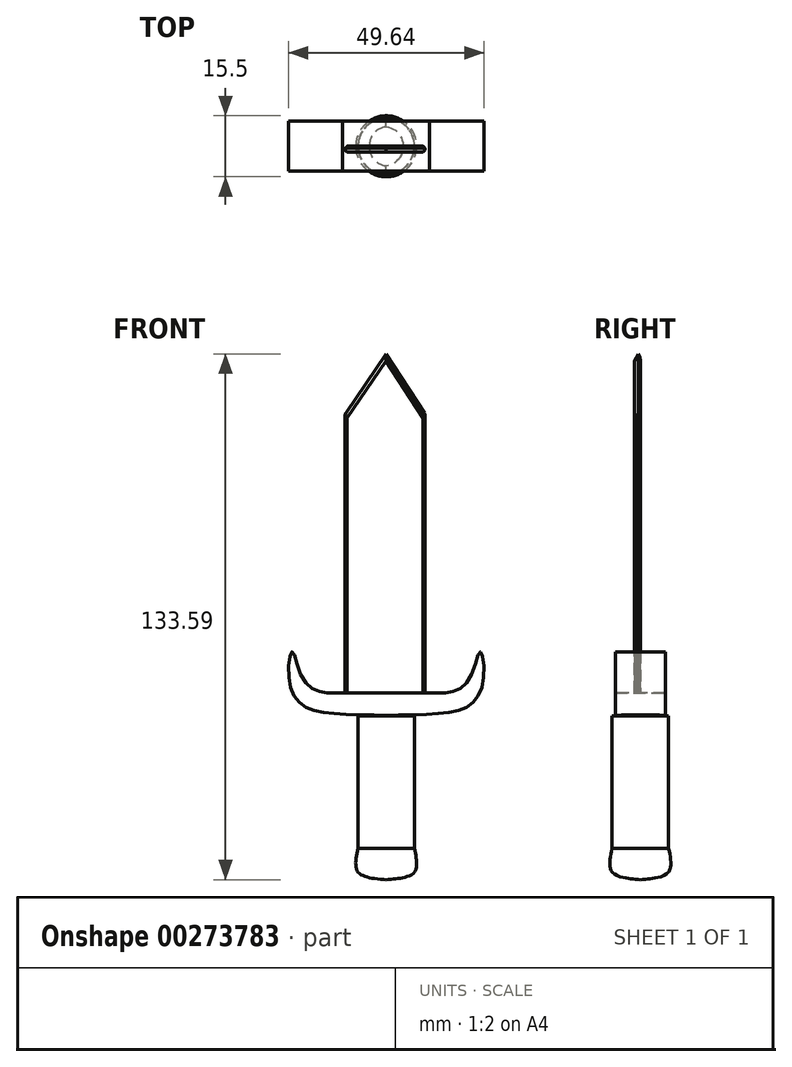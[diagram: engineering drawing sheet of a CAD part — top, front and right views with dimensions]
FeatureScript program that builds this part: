
annotation { "Feature Type Name" : "Feature", "Feature Type Description" : "" }
export const myFeature = defineFeature(function(context is Context, id is Id, definition is map)
    precondition{}
    {
        {
            var Q0;
            Q0=qCreatedBy(makeId("Front.planeOp"),FACE);
            var sketch = newSketch(context, id + "F0", { "sketchPlane" : qUnion([Q0])});
            skLineSegment(sketch, "E0", {"start": v(0, 63.6) * mm, "end": v(-10.45, 48.36) * mm});
            skLineSegment(sketch, "E1", {"start": v(-10.45, 48.36) * mm, "end": v(-10.45, 0) * mm});
            skLineSegment(sketch, "E2", {"start": v(9.85, 0) * mm, "end": v(9.85, 48.36) * mm});
            skLineSegment(sketch, "E3", {"start": v(9.85, 48.36) * mm, "end": v(0, 63.6) * mm});
            skLineSegment(sketch, "E4", {"start": v(-10.45, 0) * mm, "end": v(-10.45, -23.27) * mm});
            skLineSegment(sketch, "E5", {"start": v(-10.45, -23.27) * mm, "end": v(9.85, -23.27) * mm});
            skLineSegment(sketch, "E6", {"start": v(9.85, -23.27) * mm, "end": v(9.85, 0) * mm});
            skSolve(sketch);
        }
        {
            var Q0;
            Q0 = qSketchRegion(id + "F0", true);
            extrude(context, id + "F1", {"entities" : qUnion([Q0]), "depth" : 1.52 * mm});
        }
        {
            var Q0;
            Q0=makeQuery(id+"F1.opExtrude","CAP_EDGE",EDGE,{"disambiguationData":[OSD([sQuery(id+"F0.wireOp",EDGE,"E3")])],"isStart":true});
            var Q1;
            Q1=makeQuery(id+"F1.opExtrude","CAP_EDGE",EDGE,{"disambiguationData":[OSD([sQuery(id+"F0.wireOp",EDGE,"E0")])],"isStart":true});
            fillet(context, id + "F2", {"entities" : qUnion([Q0, Q1]), "radius" : 1.27 * mm, "tangentPropagation" : true, "allowEdgeOverflow" : false});
        }
        {
            var Q0;
            Q0=makeQuery(id+"F1.opExtrude","CAP_EDGE",EDGE,{"disambiguationData":[OSD([sQuery(id+"F0.wireOp",EDGE,"E2"),sQuery(id+"F0.wireOp",EDGE,"E6")])],"isStart":false});
            var Q1;
            Q1=makeQuery(id+"F1.opExtrude","CAP_EDGE",EDGE,{"disambiguationData":[OSD([sQuery(id+"F0.wireOp",EDGE,"E1"),sQuery(id+"F0.wireOp",EDGE,"E4")])],"isStart":false});
            chamfer(context, id + "F3", {"entities" : qUnion([Q0, Q1]), "width" : 0.5 * mm, "tangentPropagation" : true});
        }
        {
            var Q0;
            Q0=makeQuery(id+"F1.opExtrude","CAP_EDGE",EDGE,{"disambiguationData":[OSD([sQuery(id+"F0.wireOp",EDGE,"E0")])],"isStart":false});
            var Q1;
            Q1=makeQuery(id+"F1.opExtrude","CAP_EDGE",EDGE,{"disambiguationData":[OSD([sQuery(id+"F0.wireOp",EDGE,"E3")])],"isStart":false});
            chamfer(context, id + "F4", {"entities" : qUnion([Q0, Q1]), "width" : 1.27 * mm, "tangentPropagation" : true});
        }
        {
            var Q0;
            Q0=makeQuery(id+"F1.opExtrude","CAP_EDGE",EDGE,{"disambiguationData":[OSD([sQuery(id+"F0.wireOp",EDGE,"E1"),sQuery(id+"F0.wireOp",EDGE,"E4")])],"isStart":true});
            var Q1;
            Q1=makeQuery(id+"F1.opExtrude","CAP_EDGE",EDGE,{"disambiguationData":[OSD([sQuery(id+"F0.wireOp",EDGE,"E2"),sQuery(id+"F0.wireOp",EDGE,"E6")])],"isStart":true});
            chamfer(context, id + "F5", {"entities" : qUnion([Q0, Q1]), "width" : 0.5 * mm, "tangentPropagation" : true});
        }
        {
            var Q0;
            Q0=qCreatedBy(makeId("Front.planeOp"),FACE);
            var sketch = newSketch(context, id + "F6", { "sketchPlane" : qUnion([Q0])});
            skFitSpline(sketch, "E7", {"points": [v(-11.05, -22.99) * mm, v(-16.72, -22.69) * mm, v(-21.5, -18.8) * mm, v(-23.88, -12.54) * mm, v(-24.78, -18.8) * mm, v(-21.8, -25.67) * mm, v(-14.93, -28.06) * mm, v(0, -28.66) * mm], "startDerivative": vector(-46.92, -2) * mm, "endDerivative": vector(80.59, -0.6) * mm});
            skLineSegment(sketch, "E8", {"start": v(-11.05, -22.99) * mm, "end": v(0, -22.99) * mm});
            skLineSegment(sketch, "E9", {"start": v(0, -22.99) * mm, "end": v(-11.05, -22.99) * mm});
            skLineSegment(sketch, "E10", {"start": v(0, 0) * mm, "end": v(0, -40.14) * mm, "construction": true});
            skFitSpline(sketch, "E11.MirrorCS", {"points": [v(11.05, -22.99) * mm, v(16.72, -22.69) * mm, v(21.5, -18.8) * mm, v(23.88, -12.54) * mm, v(24.78, -18.8) * mm, v(21.8, -25.67) * mm, v(14.93, -28.06) * mm, v(0, -28.66) * mm], "startDerivative": vector(46.92, -2) * mm, "endDerivative": vector(-80.59, -0.6) * mm});
            skFitSpline(sketch, "E12", {"points": [v(11.05, -22.99) * mm, v(0, -22.99) * mm], "startDerivative": vector(-11.05, 0) * mm, "endDerivative": vector(-11.05, 0) * mm});
            skSolve(sketch);
        }
        {
            var Q0;
            Q0=makeQuery(id+"F6.imprint","IMPRINT",FACE,{"disambiguationData":[TD([[makeQuery(id+"F6.imprint","IMPRINT",EDGE,{"derivedFrom":sQuery(id+"F6.wireOp",EDGE,"E7")}),1.0]])]});
            extrude(context, id + "F7", {"entities" : qUnion([Q0]), "operationType" : NewBodyOperationType.ADD, "endBound" : BoundingType.SYMMETRIC, "depth" : 12.7 * mm});
        }
        {
            var Q0;
            Q0=qCreatedBy(makeId("Front.planeOp"),FACE);
            var sketch = newSketch(context, id + "F8", { "sketchPlane" : qUnion([Q0])});
            skLineSegment(sketch, "E13", {"start": v(0, -70.46) * mm, "end": v(0, -28.36) * mm});
            skLineSegment(sketch, "E14", {"start": v(-7.17, -28.8) * mm, "end": v(-7.17, -62.53) * mm});
            skFitSpline(sketch, "E15", {"points": [v(-7.17, -62.53) * mm, v(-7.17, -68.5) * mm, v(0, -70.46) * mm], "startDerivative": vector(-3.21, -14.74) * mm, "endDerivative": vector(17.17, -1.37) * mm});
            skLineSegment(sketch, "E16", {"start": v(-7.17, -28.8) * mm, "end": v(0, -28.36) * mm});
            skSolve(sketch);
        }
        {
            var Q0;
            Q0 = qSketchRegion(id + "F8", true);
            var Q1;
            Q1=sQuery(id+"F8.wireOp",EDGE,"E13");
            revolve(context, id + "F9", {"operationType" : NewBodyOperationType.ADD, "entities" : qUnion([Q0]), "axis" : qUnion([Q1]), "revolveType" : RevolveType.FULL});
        }
    });
